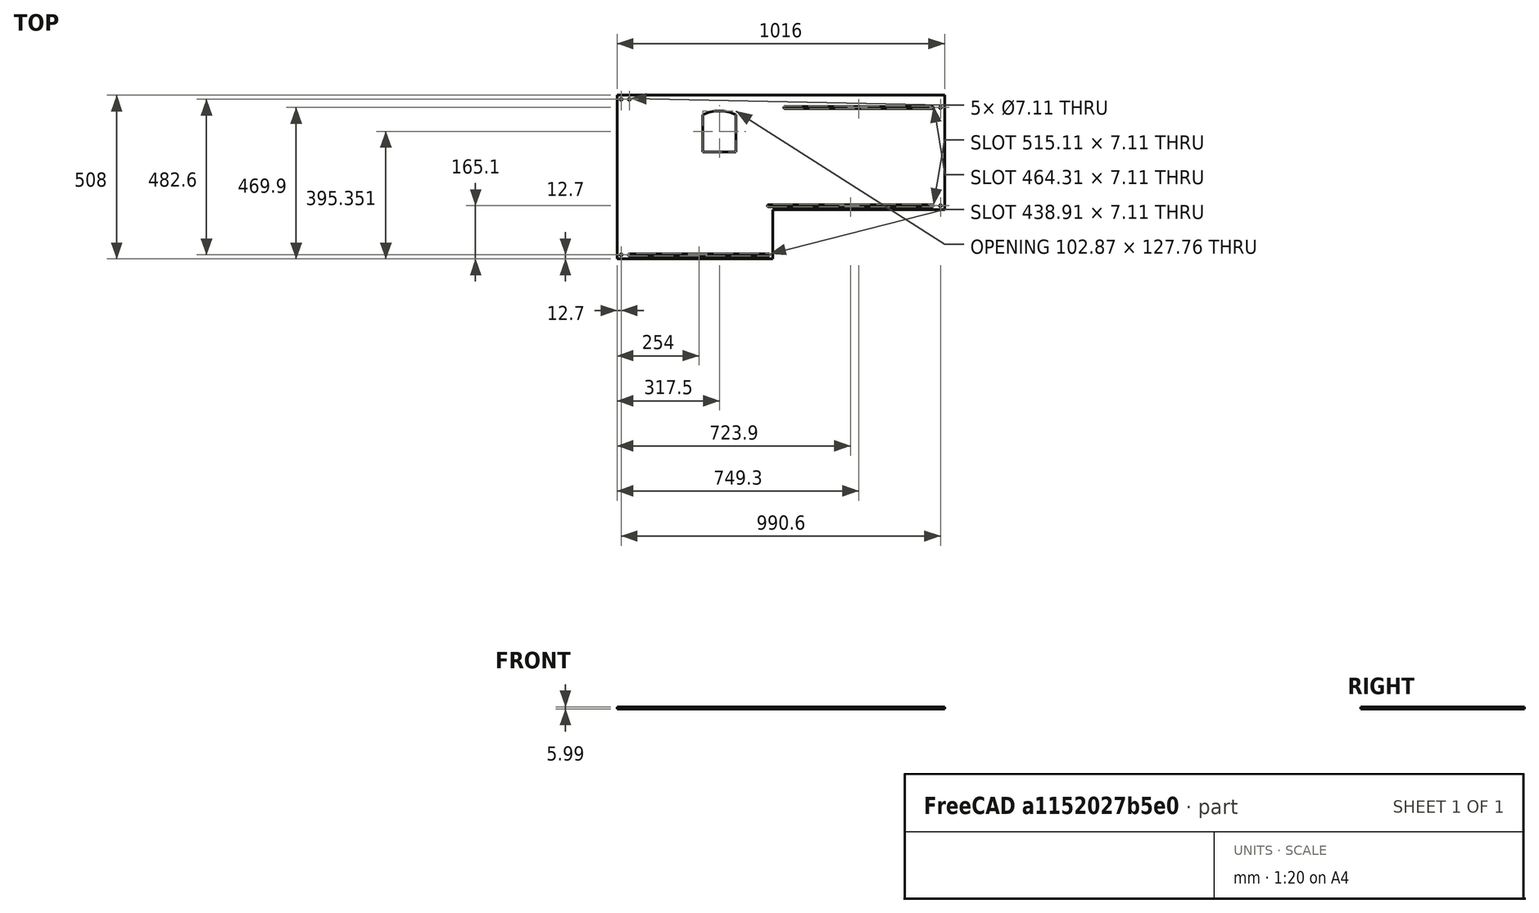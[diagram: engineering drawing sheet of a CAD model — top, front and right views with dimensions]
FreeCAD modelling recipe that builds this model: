
FCSTD DOCUMENT  (FreeCAD 0.19R24267 (Git))
Label: Up1-P9
License: All rights reserved
LicenseURL: http://en.wikipedia.org/wiki/All_rights_reserved
objects: TechDraw::DrawViewDimension×39, TechDraw::DrawProjGroupItem×2, TechDraw::DrawHatch×2, TechDraw::DrawViewAnnotation×2, Sketcher::SketchObject×1, Part::Extrusion×1, TechDraw::DrawSVGTemplate×1, TechDraw::DrawProjGroup×1, TechDraw::DrawPage×1
note: 2 computed .brp shape members not serialized (recipe doc carries the construction recipe); baked Part::Feature solids carry a one-line shape summary decoded from their .brp

FEATURE [Sketcher::SketchObject] Sketch
  FullyConstrained = true
  sketch-geometry (35):
    g0: LineSegment StartX=0 StartY=-508 StartZ=0 EndX=482.6 EndY=-508 EndZ=0
    g1: LineSegment StartX=482.6 StartY=-508 StartZ=0 EndX=482.6 EndY=-355.6 EndZ=0
    g2: LineSegment StartX=482.6 StartY=-355.6 StartZ=0 EndX=1016 EndY=-355.6 EndZ=0
    g3: LineSegment StartX=1016 StartY=-355.6 StartZ=0 EndX=1016 EndY=0 EndZ=0
    g4: LineSegment StartX=1016 StartY=0 StartZ=0 EndX=0 EndY=0 EndZ=0
    g5: LineSegment StartX=0 StartY=0 StartZ=0 EndX=0 EndY=-508 EndZ=0
    g6: LineSegment StartX=266.065 StartY=-176.53 StartZ=0 EndX=368.935 EndY=-176.53 EndZ=0
    g7: LineSegment StartX=266.065 StartY=-176.53 StartZ=0 EndX=266.065 EndY=-60.1487 EndZ=0
    g8: LineSegment StartX=368.935 StartY=-176.53 StartZ=0 EndX=368.935 EndY=-60.1487 EndZ=0
    g9: ArcOfCircle CenterX=317.5 CenterY=-170.688 CenterZ=0 NormalX=0 NormalY=0 NormalZ=1 AngleXU=0 Radius=121.92 StartAngle=1.13528 EndAngle=2.00631
    g10: Circle CenterX=12.7 CenterY=-12.7 CenterZ=0 NormalX=0 NormalY=0 NormalZ=1 AngleXU=0 Radius=3.556
    g11: Circle CenterX=38.1 CenterY=-12.7 CenterZ=0 NormalX=0 NormalY=0 NormalZ=1 AngleXU=0 Radius=3.556
    g12: Circle CenterX=1003.3 CenterY=-38.1 CenterZ=0 NormalX=0 NormalY=0 NormalZ=1 AngleXU=0 Radius=3.556
    g13: Circle CenterX=1003.3 CenterY=-342.9 CenterZ=0 NormalX=0 NormalY=0 NormalZ=1 AngleXU=0 Radius=3.556
    g14: Circle CenterX=12.7 CenterY=-495.3 CenterZ=0 NormalX=0 NormalY=0 NormalZ=1 AngleXU=0 Radius=3.556
    g15: LineSegment StartX=469.9 StartY=-346.456 StartZ=0 EndX=977.9 EndY=-346.456 EndZ=0
    g16: LineSegment StartX=520.7 StartY=-34.544 StartZ=0 EndX=977.9 EndY=-34.544 EndZ=0
    g17: LineSegment StartX=520.7 StartY=-41.656 StartZ=0 EndX=977.9 EndY=-41.656 EndZ=0
    g18: LineSegment StartX=38.1 StartY=-491.744 StartZ=0 EndX=469.9 EndY=-491.744 EndZ=0
    g19: LineSegment StartX=38.1 StartY=-498.856 StartZ=0 EndX=469.9 EndY=-498.856 EndZ=0
    g20: LineSegment StartX=977.9 StartY=-34.544 StartZ=0 EndX=977.9 EndY=-41.656 EndZ=0
    g21: ArcOfCircle CenterX=977.9 CenterY=-38.1 CenterZ=0 NormalX=0 NormalY=0 NormalZ=1 AngleXU=0 Radius=3.556 StartAngle=4.71239 EndAngle=7.85398
    g22: LineSegment StartX=520.7 StartY=-34.544 StartZ=0 EndX=520.7 EndY=-41.656 EndZ=0
    g23: ArcOfCircle CenterX=520.7 CenterY=-38.1 CenterZ=0 NormalX=0 NormalY=0 NormalZ=1 AngleXU=0 Radius=3.556 StartAngle=1.5708 EndAngle=4.71239
    g24: LineSegment StartX=38.1 StartY=-491.744 StartZ=0 EndX=38.1 EndY=-498.856 EndZ=0
    g25: LineSegment StartX=469.9 StartY=-491.744 StartZ=0 EndX=469.9 EndY=-498.856 EndZ=0
    g26: ArcOfCircle CenterX=38.1 CenterY=-495.3 CenterZ=0 NormalX=0 NormalY=0 NormalZ=1 AngleXU=0 Radius=3.556 StartAngle=1.5708 EndAngle=4.71239
    g27: ArcOfCircle CenterX=469.9 CenterY=-495.3 CenterZ=0 NormalX=0 NormalY=0 NormalZ=1 AngleXU=0 Radius=3.556 StartAngle=4.71239 EndAngle=7.85398
    g28: LineSegment StartX=469.9 StartY=-339.344 StartZ=0 EndX=469.9 EndY=-346.456 EndZ=0
    g29: ArcOfCircle CenterX=469.9 CenterY=-342.9 CenterZ=0 NormalX=0 NormalY=0 NormalZ=1 AngleXU=0 Radius=3.556 StartAngle=1.5708 EndAngle=4.71239
    g30: ArcOfCircle CenterX=977.9 CenterY=-342.9 CenterZ=0 NormalX=0 NormalY=0 NormalZ=1 AngleXU=0 Radius=3.556 StartAngle=4.71239 EndAngle=7.85398
    g31: LineSegment StartX=469.9 StartY=-339.344 StartZ=0 EndX=977.9 EndY=-339.344 EndZ=0
    g32: LineSegment StartX=977.9 StartY=-346.456 StartZ=0 EndX=977.9 EndY=-339.344 EndZ=0
    g33: LineSegment StartX=977.9 StartY=-342.9 StartZ=0 EndX=1003.3 EndY=-342.9 EndZ=0
    g34: LineSegment StartX=38.1 StartY=-495.3 StartZ=0 EndX=12.7 EndY=-495.3 EndZ=0
  constraints (103):
    c: Horizontal(g0)
    c: Coincident(g1,g0)
    c: Vertical(g1)
    c: DistanceY(g1,g1) = 152.4
    c: Coincident(g2,g1)
    c: Horizontal(g2)
    c: Coincident(g3,g2)
    c: Vertical(g3)
    c: DistanceY(g3,g3) = 355.6
    c: Coincident(g4,g3)
    c: Horizontal(g4)
    c: DistanceX(g4,g4) = 1016
    c: Coincident(g5,g4)
    c: Coincident(g5,g0)
    c: Horizontal(g6)
    c: DistanceX(g6,g6) = 102.87
    c: Coincident(g7,g6)
    c: Vertical(g7)
    c: Coincident(g8,g6)
    c: Vertical(g8)
    c: Distance(g6,g5) = 266.065
    c: Distance(g6,g4) = 176.53
    c: Coincident(g9,g8)
    c: Coincident(g9,g7)
    c: Radius(g9) = 121.92
    c: Distance(g9,g5) = 317.5
    c: Distance(g9,g4) = 170.688
    c: Distance(g10,g5) = 12.7
    c: Distance(g10,g4) = 12.7
    c: Distance(g11,g4) = 12.7
    c: Distance(g14,g5) = 12.7
    c: Horizontal(g15)
    c: Horizontal(g16)
    c: Horizontal(g17)
    c: Horizontal(g18)
    c: Horizontal(g19)
    c: Diameter(g10) = 7.112
    c: Coincident(g20,g16)
    c: Coincident(g20,g17)
    c: Vertical(g20)
    c: PointOnObject(g21,g20)
    c: Coincident(g21,g16)
    c: Coincident(g21,g17)
    c: Coincident(g22,g16)
    c: Coincident(g22,g17)
    c: PointOnObject(g23,g22)
    c: Coincident(g23,g16)
    c: Coincident(g23,g17)
    c: Distance(g23,g21) = 457.2
    c: Distance(g21,g4) = 38.1
    c: Distance(g21,g3) = 38.1
    c: Horizontal(g12,g21)
    c: Coincident(g24,g18)
    c: Coincident(g24,g19)
    c: Vertical(g24)
    c: Coincident(g25,g18)
    c: Coincident(g25,g19)
    c: PointOnObject(g26,g24)
    c: Coincident(g26,g18)
    c: Coincident(g26,g19)
    c: PointOnObject(g27,g25)
    c: Coincident(g27,g18)
    c: Coincident(g27,g19)
    c: Distance(g26,g27) = 431.8
    c: Horizontal(g14,g26)
    c: Distance(g14,g0) = 12.7
    c: Distance(g0,g24) = 38.1
    c: Coincident(g-1,g4)
    c: Vertical(g25)
    c: Coincident(g28,g15)
    c: Vertical(g28)
    c: PointOnObject(g29,g28)
    c: Coincident(g29,g15)
    c: Coincident(g30,g15)
    c: Distance(g30,g3) = 38.1
    c: Coincident(g31,g29)
    c: Coincident(g31,g30)
    c: Horizontal(g31)
    c: Coincident(g29,g28)
    c: Coincident(g32,g15)
    c: Vertical(g32)
    c: Coincident(g30,g32)
    c: PointOnObject(g30,g32)
    c: Distance(g30,g29) = 508
    c: Equal(g11,g10)
    c: Equal(g14,g10)
    c: Equal(g12,g10)
    c: Equal(g13,g10)
    c: Distance(g12,g3) = 12.7
    c: Equal(g17,g16)
    c: Distance(g13,g2) = 12.7
    c: Distance(g13,g3) = 12.7
    c: Distance(g11,g5) = 38.1
    c: Vertical(g5)
    c: Distance(g2,g1) = 533.4
    c: Equal(g12,g21)
    c: Equal(g30,g13)
    c: Coincident(g33,g30)
    c: Coincident(g33,g13)
    c: Horizontal(g33)
    c: Coincident(g34,g26)
    c: Coincident(g34,g14)
    c: Equal(g14,g26)
FEATURE [Part::Extrusion] Extrude
  Base = -> Sketch
  Dir = (0,0,1)
  DirMode = 2
  FaceMakerClass = Part::FaceMakerBullseye
  LengthFwd = 5.9944
  LengthRev = 0
  Solid = true
  Symmetric = false
FEATURE [TechDraw::DrawSVGTemplate] Template
  Height = 215.9
  Orientation = 1
  Width = 279.4
FEATURE [TechDraw::DrawProjGroupItem] ProjItem  label="Front"
  CoarseView = false
  Direction = (0,0,1)
  Focus = 100
  HardHidden = false
  IsoCount = 0
  IsoHidden = false
  IsoVisible = false
  LockPosition = true
  Perspective = false
  Rotation = 0
  RotationVector = (-1,0,0)
  Scale = 0.2
  ScaleType = 2
  SeamHidden = false
  SeamVisible = true
  SmoothHidden = false
  SmoothVisible = true
  Source = -> [Extrude]
  Type = 0
  X = 0
  XDirection = (-1,0,0)
  Y = 0
FEATURE [TechDraw::DrawProjGroupItem] ProjItem001  label="Left"
  CoarseView = false
  Direction = (1,0,1e-16)
  Focus = 100
  HardHidden = false
  IsoCount = 0
  IsoHidden = false
  IsoVisible = false
  LockPosition = false
  Perspective = false
  Rotation = 0
  RotationVector = (1,0,0)
  Scale = 0.2
  ScaleType = 2
  SeamHidden = false
  SeamVisible = true
  SmoothHidden = false
  SmoothVisible = true
  Source = -> [Extrude]
  Type = 1
  X = 132.435
  XDirection = (-1e-16,0,1)
  Y = 0
FEATURE [TechDraw::DrawProjGroup] ProjGroup
  Anchor = -> ProjItem
  AutoDistribute = true
  LockPosition = false
  ProjectionType = 0
  Rotation = 0
  Scale = 0.2
  ScaleType = 2
  Source = -> [Extrude]
  Views = -> [ProjItem,ProjItem001]
  X = 130.707
  Y = 107.127
  spacingX = 15.0114
  spacingY = 15.0114
FEATURE [TechDraw::DrawHatch] Hatch  label="HatchF0"
  HatchPattern = <path>
  Source = -> ProjItem [Face0]
FEATURE [TechDraw::DrawHatch] Hatch001  label="Hatch001F1"
  HatchPattern = <path>
  Source = -> ProjItem001 [Face1,Face2]
FEATURE [TechDraw::DrawViewDimension] Dimension
  Arbitrary = false
  ArbitraryTolerances = false
  EqualTolerance = true
  FormatSpec = %.3f
  FormatSpecOverTolerance = %+.3f
  FormatSpecUnderTolerance = %+.3f
  Inverted = false
  LockPosition = false
  MeasureType = 1
  OverTolerance = 0
  References2D = -> [ProjItem]
  Rotation = 0
  ScaleType = 0
  TheoreticalExact = false
  Type = 2
  UnderTolerance = 0
  X = 116.065
  Y = 1.62593
FEATURE [TechDraw::DrawViewDimension] Dimension001
  Arbitrary = false
  ArbitraryTolerances = false
  EqualTolerance = true
  FormatSpec = %.3f
  FormatSpecOverTolerance = %+.3f
  FormatSpecUnderTolerance = %+.3f
  Inverted = false
  LockPosition = false
  MeasureType = 1
  OverTolerance = 0
  References2D = -> [ProjItem001]
  Rotation = 0
  ScaleType = 0
  TheoreticalExact = false
  Type = 1
  UnderTolerance = 0
  X = -12.0718
  Y = 70.5398
FEATURE [TechDraw::DrawViewDimension] Dimension002
  Arbitrary = false
  ArbitraryTolerances = false
  EqualTolerance = true
  FormatSpec = %.3f
  FormatSpecOverTolerance = %+.3f
  FormatSpecUnderTolerance = %+.3f
  Inverted = false
  LockPosition = false
  MeasureType = 1
  OverTolerance = 0
  References2D = -> [ProjItem]
  Rotation = 0
  ScaleType = 0
  TheoreticalExact = false
  Type = 1
  UnderTolerance = 0
  X = 56.5327
  Y = 97.201
FEATURE [TechDraw::DrawViewDimension] Dimension003
  Arbitrary = false
  ArbitraryTolerances = false
  EqualTolerance = true
  FormatSpec = ⌀%.3f
  FormatSpecOverTolerance = %+.3f
  FormatSpecUnderTolerance = %+.3f
  Inverted = false
  LockPosition = false
  MeasureType = 1
  OverTolerance = 0
  References2D = -> [ProjItem]
  Rotation = 0
  ScaleType = 0
  TheoreticalExact = false
  Type = 5
  UnderTolerance = 0
  X = 92.673
  Y = 75.4491
FEATURE [TechDraw::DrawViewDimension] Dimension004
  Arbitrary = false
  ArbitraryTolerances = false
  EqualTolerance = true
  FormatSpec = ⌀%.3f
  FormatSpecOverTolerance = %+.3f
  FormatSpecUnderTolerance = %+.3f
  Inverted = false
  LockPosition = false
  MeasureType = 1
  OverTolerance = 0
  References2D = -> [ProjItem]
  Rotation = 0
  ScaleType = 0
  TheoreticalExact = false
  Type = 5
  UnderTolerance = 0
  X = -112.88
  Y = 8.5031
FEATURE [TechDraw::DrawViewDimension] Dimension005
  Arbitrary = false
  ArbitraryTolerances = false
  EqualTolerance = true
  FormatSpec = ⌀%.3f
  FormatSpecOverTolerance = %+.3f
  FormatSpecUnderTolerance = %+.3f
  Inverted = false
  LockPosition = false
  MeasureType = 1
  OverTolerance = 0
  References2D = -> [ProjItem]
  Rotation = 0
  ScaleType = 0
  TheoreticalExact = false
  Type = 5
  UnderTolerance = 0
  X = -108.827
  Y = 3.37717
FEATURE [TechDraw::DrawViewDimension] Dimension006
  Arbitrary = false
  ArbitraryTolerances = false
  EqualTolerance = true
  FormatSpec = %.3f
  FormatSpecOverTolerance = %+.3f
  FormatSpecUnderTolerance = %+.3f
  Inverted = false
  LockPosition = false
  MeasureType = 1
  OverTolerance = 0
  References2D = -> [ProjItem]
  Rotation = 0
  ScaleType = 0
  TheoreticalExact = false
  Type = 1
  UnderTolerance = 0
  X = -43.5271
  Y = 8.66456
FEATURE [TechDraw::DrawViewDimension] Dimension007
  Arbitrary = false
  ArbitraryTolerances = false
  EqualTolerance = true
  FormatSpec = ⌀%.3f
  FormatSpecOverTolerance = %+.3f
  FormatSpecUnderTolerance = %+.3f
  Inverted = false
  LockPosition = false
  MeasureType = 1
  OverTolerance = 0
  References2D = -> [ProjItem]
  Rotation = 0
  ScaleType = 0
  TheoreticalExact = false
  Type = 5
  UnderTolerance = 0
  X = 23.7681
  Y = 12.4162
FEATURE [TechDraw::DrawViewDimension] Dimension008
  Arbitrary = false
  ArbitraryTolerances = false
  EqualTolerance = true
  FormatSpec = %.3f
  FormatSpecOverTolerance = %+.3f
  FormatSpecUnderTolerance = %+.3f
  Inverted = false
  LockPosition = false
  MeasureType = 1
  OverTolerance = 0
  References2D = -> [ProjItem]
  Rotation = 0
  ScaleType = 0
  TheoreticalExact = false
  Type = 1
  UnderTolerance = 0
  X = 50.6876
  Y = 40.2416
FEATURE [TechDraw::DrawViewDimension] Dimension009
  Arbitrary = false
  ArbitraryTolerances = false
  EqualTolerance = true
  FormatSpec = ⌀%.3f
  FormatSpecOverTolerance = %+.3f
  FormatSpecUnderTolerance = %+.3f
  Inverted = false
  LockPosition = false
  MeasureType = 1
  OverTolerance = 0
  References2D = -> [ProjItem]
  Rotation = 0
  ScaleType = 0
  TheoreticalExact = false
  Type = 5
  UnderTolerance = 0
  X = -2.00262
  Y = 64.639
FEATURE [TechDraw::DrawViewDimension] Dimension010
  Arbitrary = false
  ArbitraryTolerances = false
  EqualTolerance = true
  FormatSpec = ⌀%.3f
  FormatSpecOverTolerance = %+.3f
  FormatSpecUnderTolerance = %+.3f
  Inverted = false
  LockPosition = false
  MeasureType = 1
  OverTolerance = 0
  References2D = -> [ProjItem]
  Rotation = 0
  ScaleType = 0
  TheoreticalExact = false
  Type = 5
  UnderTolerance = 0
  X = 86.0555
  Y = 72.2732
FEATURE [TechDraw::DrawViewDimension] Dimension011
  Arbitrary = false
  ArbitraryTolerances = false
  EqualTolerance = true
  FormatSpec = %.3f
  FormatSpecOverTolerance = %+.3f
  FormatSpecUnderTolerance = %+.3f
  Inverted = false
  LockPosition = false
  MeasureType = 1
  OverTolerance = 0
  References2D = -> [ProjItem]
  Rotation = 0
  ScaleType = 0
  TheoreticalExact = false
  Type = 2
  UnderTolerance = 0
  X = 70.744
  Y = 64.2236
FEATURE [TechDraw::DrawViewDimension] Dimension012
  Arbitrary = false
  ArbitraryTolerances = false
  EqualTolerance = true
  FormatSpec = ⌀%.3f
  FormatSpecOverTolerance = %+.3f
  FormatSpecUnderTolerance = %+.3f
  Inverted = false
  LockPosition = false
  MeasureType = 1
  OverTolerance = 0
  References2D = -> [ProjItem]
  Rotation = 0
  ScaleType = 0
  TheoreticalExact = false
  Type = 5
  UnderTolerance = 0
  X = 122.178
  Y = -61.7884
FEATURE [TechDraw::DrawViewDimension] Dimension013
  Arbitrary = false
  ArbitraryTolerances = false
  EqualTolerance = true
  FormatSpec = ⌀%.3f
  FormatSpecOverTolerance = %+.3f
  FormatSpecUnderTolerance = %+.3f
  Inverted = false
  LockPosition = false
  MeasureType = 1
  OverTolerance = 0
  References2D = -> [ProjItem]
  Rotation = 0
  ScaleType = 0
  TheoreticalExact = false
  Type = 5
  UnderTolerance = 0
  X = 117.281
  Y = -65.9854
FEATURE [TechDraw::DrawViewDimension] Dimension014
  Arbitrary = false
  ArbitraryTolerances = false
  EqualTolerance = true
  FormatSpec = R%.3f
  FormatSpecOverTolerance = %+.3f
  FormatSpecUnderTolerance = %+.3f
  Inverted = false
  LockPosition = false
  MeasureType = 1
  OverTolerance = 0
  References2D = -> [ProjItem]
  Rotation = 0
  ScaleType = 0
  TheoreticalExact = false
  Type = 4
  UnderTolerance = 0
  X = 22.8501
  Y = -62.2548
FEATURE [TechDraw::DrawViewDimension] Dimension015
  Arbitrary = false
  ArbitraryTolerances = false
  EqualTolerance = true
  FormatSpec = %.3f
  FormatSpecOverTolerance = %+.3f
  FormatSpecUnderTolerance = %+.3f
  Inverted = false
  LockPosition = false
  MeasureType = 1
  OverTolerance = 0
  References2D = -> [ProjItem]
  Rotation = 0
  ScaleType = 0
  TheoreticalExact = false
  Type = 1
  UnderTolerance = 0
  X = 37.0475
  Y = 0.061869
FEATURE [TechDraw::DrawViewDimension] Dimension017
  Arbitrary = false
  ArbitraryTolerances = false
  EqualTolerance = true
  FormatSpec = %.3f
  FormatSpecOverTolerance = %+.3f
  FormatSpecUnderTolerance = %+.3f
  Inverted = false
  LockPosition = false
  MeasureType = 1
  OverTolerance = 0
  References2D = -> [ProjItem]
  Rotation = 0
  ScaleType = 0
  TheoreticalExact = false
  Type = 2
  UnderTolerance = 0
  X = 14.8633
  Y = -30.6638
FEATURE [TechDraw::DrawViewDimension] Dimension018
  Arbitrary = false
  ArbitraryTolerances = false
  EqualTolerance = true
  FormatSpec = %.3f
  FormatSpecOverTolerance = %+.3f
  FormatSpecUnderTolerance = %+.3f
  Inverted = false
  LockPosition = false
  MeasureType = 1
  OverTolerance = 0
  References2D = -> [ProjItem]
  Rotation = 0
  ScaleType = 0
  TheoreticalExact = false
  Type = 2
  UnderTolerance = 0
  X = 21.6042
  Y = -30.7158
FEATURE [TechDraw::DrawViewDimension] Dimension019
  Arbitrary = false
  ArbitraryTolerances = false
  EqualTolerance = true
  FormatSpec = %.3f
  FormatSpecOverTolerance = %+.3f
  FormatSpecUnderTolerance = %+.3f
  Inverted = false
  LockPosition = false
  MeasureType = 1
  OverTolerance = 0
  References2D = -> [ProjItem]
  Rotation = 0
  ScaleType = 0
  TheoreticalExact = false
  Type = 1
  UnderTolerance = 0
  X = 74.8161
  Y = -0.594599
FEATURE [TechDraw::DrawViewDimension] Dimension020
  Arbitrary = false
  ArbitraryTolerances = false
  EqualTolerance = true
  FormatSpec = ⌀%.3f
  FormatSpecOverTolerance = %+.3f
  FormatSpecUnderTolerance = %+.3f
  Inverted = false
  LockPosition = false
  MeasureType = 1
  OverTolerance = 0
  References2D = -> [ProjItem]
  Rotation = 0
  ScaleType = 0
  TheoreticalExact = false
  Type = 5
  UnderTolerance = 0
  X = -115.911
  Y = -21.5426
FEATURE [TechDraw::DrawViewDimension] Dimension021
  Arbitrary = false
  ArbitraryTolerances = false
  EqualTolerance = true
  FormatSpec = ⌀%.3f
  FormatSpecOverTolerance = %+.3f
  FormatSpecUnderTolerance = %+.3f
  Inverted = false
  LockPosition = false
  MeasureType = 1
  OverTolerance = 0
  References2D = -> [ProjItem]
  Rotation = 0
  ScaleType = 0
  TheoreticalExact = false
  Type = 5
  UnderTolerance = 0
  X = -113.956
  Y = -13.8372
FEATURE [TechDraw::DrawViewDimension] Dimension022
  Arbitrary = false
  ArbitraryTolerances = false
  EqualTolerance = true
  FormatSpec = %.3f
  FormatSpecOverTolerance = %+.3f
  FormatSpecUnderTolerance = %+.3f
  Inverted = false
  LockPosition = false
  MeasureType = 1
  OverTolerance = 0
  References2D = -> [ProjItem]
  Rotation = 0
  ScaleType = 0
  TheoreticalExact = false
  Type = 1
  UnderTolerance = 0
  X = -44.8384
  Y = -24.1903
FEATURE [TechDraw::DrawViewDimension] Dimension023
  Arbitrary = false
  ArbitraryTolerances = false
  EqualTolerance = true
  FormatSpec = ⌀%.3f
  FormatSpecOverTolerance = %+.3f
  FormatSpecUnderTolerance = %+.3f
  Inverted = false
  LockPosition = false
  MeasureType = 1
  OverTolerance = 0
  References2D = -> [ProjItem]
  Rotation = 0
  ScaleType = 0
  TheoreticalExact = false
  Type = 5
  UnderTolerance = 0
  X = 1.16582
  Y = -28.2128
FEATURE [TechDraw::DrawViewDimension] Dimension024
  Arbitrary = false
  ArbitraryTolerances = false
  EqualTolerance = true
  FormatSpec = %.3f
  FormatSpecOverTolerance = %+.3f
  FormatSpecUnderTolerance = %+.3f
  Inverted = false
  LockPosition = false
  MeasureType = 1
  OverTolerance = 0
  References2D = -> [ProjItem]
  Rotation = 0
  ScaleType = 0
  TheoreticalExact = false
  Type = 2
  UnderTolerance = 0
  X = -117.623
  Y = -56.8568
FEATURE [TechDraw::DrawViewDimension] Dimension025
  Arbitrary = false
  ArbitraryTolerances = false
  EqualTolerance = true
  FormatSpec = %.3f
  FormatSpecOverTolerance = %+.3f
  FormatSpecUnderTolerance = %+.3f
  Inverted = false
  LockPosition = false
  MeasureType = 1
  OverTolerance = 0
  References2D = -> [ProjItem]
  Rotation = 0
  ScaleType = 0
  TheoreticalExact = false
  Type = 1
  UnderTolerance = 0
  X = -80.5252
  Y = -51.6139
FEATURE [TechDraw::DrawViewDimension] Dimension026
  Arbitrary = false
  ArbitraryTolerances = false
  EqualTolerance = true
  FormatSpec = %.3f
  FormatSpecOverTolerance = %+.3f
  FormatSpecUnderTolerance = %+.3f
  Inverted = false
  LockPosition = false
  MeasureType = 1
  OverTolerance = 0
  References2D = -> [ProjItem]
  Rotation = 0
  ScaleType = 0
  TheoreticalExact = false
  Type = 1
  UnderTolerance = 0
  X = -80.9395
  Y = -58.5524
FEATURE [TechDraw::DrawViewDimension] Dimension027
  Arbitrary = false
  ArbitraryTolerances = false
  EqualTolerance = true
  FormatSpec = %.3f
  FormatSpecOverTolerance = %+.3f
  FormatSpecUnderTolerance = %+.3f
  Inverted = false
  LockPosition = false
  MeasureType = 1
  OverTolerance = 0
  References2D = -> [ProjItem]
  Rotation = 0
  ScaleType = 0
  TheoreticalExact = false
  Type = 2
  UnderTolerance = 0
  X = -117.453
  Y = 33.6677
FEATURE [TechDraw::DrawViewDimension] Dimension028
  Arbitrary = false
  ArbitraryTolerances = false
  EqualTolerance = true
  FormatSpec = %.3f
  FormatSpecOverTolerance = %+.3f
  FormatSpecUnderTolerance = %+.3f
  Inverted = false
  LockPosition = false
  MeasureType = 1
  OverTolerance = 0
  References2D = -> [ProjItem]
  Rotation = 0
  ScaleType = 0
  TheoreticalExact = false
  Type = 1
  UnderTolerance = 0
  X = -112.233
  Y = 57.0237
FEATURE [TechDraw::DrawViewDimension] Dimension029
  Arbitrary = false
  ArbitraryTolerances = false
  EqualTolerance = true
  FormatSpec = %.3f
  FormatSpecOverTolerance = %+.3f
  FormatSpecUnderTolerance = %+.3f
  Inverted = false
  LockPosition = false
  MeasureType = 1
  OverTolerance = 0
  References2D = -> [ProjItem]
  Rotation = 0
  ScaleType = 0
  TheoreticalExact = false
  Type = 1
  UnderTolerance = 0
  X = -112.403
  Y = 48.8245
FEATURE [TechDraw::DrawViewDimension] Dimension030
  Arbitrary = false
  ArbitraryTolerances = false
  EqualTolerance = true
  FormatSpec = %.3f
  FormatSpecOverTolerance = %+.3f
  FormatSpecUnderTolerance = %+.3f
  Inverted = false
  LockPosition = false
  MeasureType = 1
  OverTolerance = 0
  References2D = -> [ProjItem]
  Rotation = 0
  ScaleType = 0
  TheoreticalExact = false
  Type = 2
  UnderTolerance = 0
  X = -20.9141
  Y = 37.1701
FEATURE [TechDraw::DrawViewDimension] Dimension032
  Arbitrary = false
  ArbitraryTolerances = false
  EqualTolerance = true
  FormatSpec = %.3f
  FormatSpecOverTolerance = %+.3f
  FormatSpecUnderTolerance = %+.3f
  Inverted = false
  LockPosition = false
  MeasureType = 1
  OverTolerance = 0
  References2D = -> [ProjItem]
  Rotation = 0
  ScaleType = 0
  TheoreticalExact = false
  Type = 1
  UnderTolerance = 0
  X = -1.47121
  Y = -70.6613
FEATURE [TechDraw::DrawViewDimension] Dimension034
  Arbitrary = false
  ArbitraryTolerances = false
  EqualTolerance = true
  FormatSpec = %.3f
  FormatSpecOverTolerance = %+.3f
  FormatSpecUnderTolerance = %+.3f
  Inverted = false
  LockPosition = false
  MeasureType = 1
  OverTolerance = 0
  References2D = -> [ProjItem]
  Rotation = 0
  ScaleType = 0
  TheoreticalExact = false
  Type = 1
  UnderTolerance = 0
  X = 112.303
  Y = 36.1395
FEATURE [TechDraw::DrawViewDimension] Dimension035
  Arbitrary = false
  ArbitraryTolerances = false
  EqualTolerance = true
  FormatSpec = %.3f
  FormatSpecOverTolerance = %+.3f
  FormatSpecUnderTolerance = %+.3f
  Inverted = false
  LockPosition = false
  MeasureType = 1
  OverTolerance = 0
  References2D = -> [ProjItem]
  Rotation = 0
  ScaleType = 0
  TheoreticalExact = false
  Type = 2
  UnderTolerance = 0
  X = 107.426
  Y = 68.7503
FEATURE [TechDraw::DrawViewDimension] Dimension036
  Arbitrary = false
  ArbitraryTolerances = false
  EqualTolerance = true
  FormatSpec = %.3f
  FormatSpecOverTolerance = %+.3f
  FormatSpecUnderTolerance = %+.3f
  Inverted = false
  LockPosition = false
  MeasureType = 1
  OverTolerance = 0
  References2D = -> [ProjItem]
  Rotation = 0
  ScaleType = 0
  TheoreticalExact = false
  Type = 1
  UnderTolerance = 0
  X = 112.335
  Y = 27.6846
FEATURE [TechDraw::DrawViewAnnotation] Annotation
  Font = osifont
  LineSpace = 80
  LockPosition = false
  MaxWidth = -1
  Rotation = 0
  ScaleType = 0
  Text = Figure S3 (Upright) | Panel 9 [top] | Quantity: 1
  TextSize = 5.0038
  TextStyle = 0
  X = 29.5084
  Y = 195.58
FEATURE [TechDraw::DrawViewAnnotation] Annotation002
  Font = osifont
  LineSpace = 80
  LockPosition = false
  MaxWidth = -1
  Rotation = 0
  ScaleType = 0
  Text = Units: Inches
  TextSize = 5.0038
  TextStyle = 0
  X = 259.08
  Y = 5.08
FEATURE [TechDraw::DrawViewDimension] Dimension037
  Arbitrary = false
  ArbitraryTolerances = false
  EqualTolerance = true
  FormatSpec = %.3f
  FormatSpecOverTolerance = %+.3f
  FormatSpecUnderTolerance = %+.3f
  Inverted = false
  LockPosition = false
  MeasureType = 1
  OverTolerance = 0
  References2D = -> [ProjItem]
  Rotation = 0
  ScaleType = 0
  TheoreticalExact = false
  Type = 2
  UnderTolerance = 0
  X = -30.8759
  Y = -59.6418
FEATURE [TechDraw::DrawViewDimension] Dimension038
  Arbitrary = false
  ArbitraryTolerances = false
  EqualTolerance = true
  FormatSpec = %.3f
  FormatSpecOverTolerance = %+.3f
  FormatSpecUnderTolerance = %+.3f
  Inverted = false
  LockPosition = false
  MeasureType = 1
  OverTolerance = 0
  References2D = -> [ProjItem]
  Rotation = 0
  ScaleType = 0
  TheoreticalExact = false
  Type = 2
  UnderTolerance = 0
  X = -67.9117
  Y = 33.1524
FEATURE [TechDraw::DrawViewDimension] Dimension039
  Arbitrary = false
  ArbitraryTolerances = false
  EqualTolerance = true
  FormatSpec = %.3f
  FormatSpecOverTolerance = %+.3f
  FormatSpecUnderTolerance = %+.3f
  Inverted = false
  LockPosition = false
  MeasureType = 1
  OverTolerance = 0
  References2D = -> [ProjItem]
  Rotation = 0
  ScaleType = 0
  TheoreticalExact = false
  Type = 2
  UnderTolerance = 0
  X = 81.5947
  Y = -64.2643
FEATURE [TechDraw::DrawViewDimension] Dimension040
  Arbitrary = false
  ArbitraryTolerances = false
  EqualTolerance = true
  FormatSpec = %.3f
  FormatSpecOverTolerance = %+.3f
  FormatSpecUnderTolerance = %+.3f
  Inverted = false
  LockPosition = false
  MeasureType = 1
  OverTolerance = 0
  References2D = -> [ProjItem]
  Rotation = 0
  ScaleType = 0
  TheoreticalExact = false
  Type = 1
  UnderTolerance = 0
  X = 80.2105
  Y = -14.9812
FEATURE [TechDraw::DrawViewDimension] Dimension041
  Arbitrary = false
  ArbitraryTolerances = false
  EqualTolerance = true
  FormatSpec = %.3f
  FormatSpecOverTolerance = %+.3f
  FormatSpecUnderTolerance = %+.3f
  Inverted = false
  LockPosition = false
  MeasureType = 1
  OverTolerance = 0
  References2D = -> [ProjItem]
  Rotation = 0
  ScaleType = 0
  TheoreticalExact = false
  Type = 1
  UnderTolerance = 0
  X = 112.175
  Y = -31.1506
FEATURE [TechDraw::DrawPage] Page
  KeepUpdated = true
  NextBalloonIndex = 1
  ProjectionType = 0
  Template = -> Template
  Views = -> [ProjGroup,Dimension,Dimension001,Dimension002,Dimension003,Dimension004,Dimension005,Dimension006,Dimension007,Dimension008,Dimension009,Dimension010,Dimension011,Dimension012,Dimension013,Dimension014,Dimension015,Dimension017,Dimension018,Dimension019,Dimension020,Dimension021,Dimension022,Dimension023,Dimension024,Dimension025,Dimension026,Dimension027,Dimension028,Dimension029,Dimension030,+11 more]
note: 2 file-system paths scrubbed to <path> (originals preserved in the JSON sidecar)
